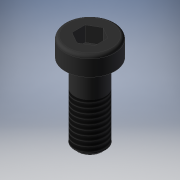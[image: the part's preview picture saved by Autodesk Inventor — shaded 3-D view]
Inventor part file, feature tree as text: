
AUTODESK INVENTOR PART (.ipt)
format: ipt  version: 2019 (Build 230136000, 136)  size: 143,360 bytes
history: native  units: mm
features: other x7, sketch x2, revolve x1, thread x1, extrude x1
ambient origin geometry x8: Origin, YZ Plane, XZ Plane, XY Plane, X Axis, Y Axis, Z Axis, Center Point
bodies: Solid1 (feature_tree)
feature tree (12):
  revolve  "Revolution1"  [1 undecoded]
  thread  "Thread1"  [1 undecoded]
  extrude  "Extrusion1"  [1 undecoded]
  other  "p1_XY"
  other  "p1_YZ"
  other  "p1_ZX"
  other  "p1_X"
  other  "p1_Y"
  other  "p1_Z"
  other  "p1_Center"
  sketch  "Sketch_1"  dims[d0=360.0deg d1=12.233mm d2=0.0mm d3=4.0mm d4=0.0mm]
  sketch  "Sketch_2"  dims[d5=0.0mm]
note: 3 required parameter values undecoded (feature->parameter linkage not recoverable at this tier; creation-order binding heuristic only, values carry confidence <= 0.55)